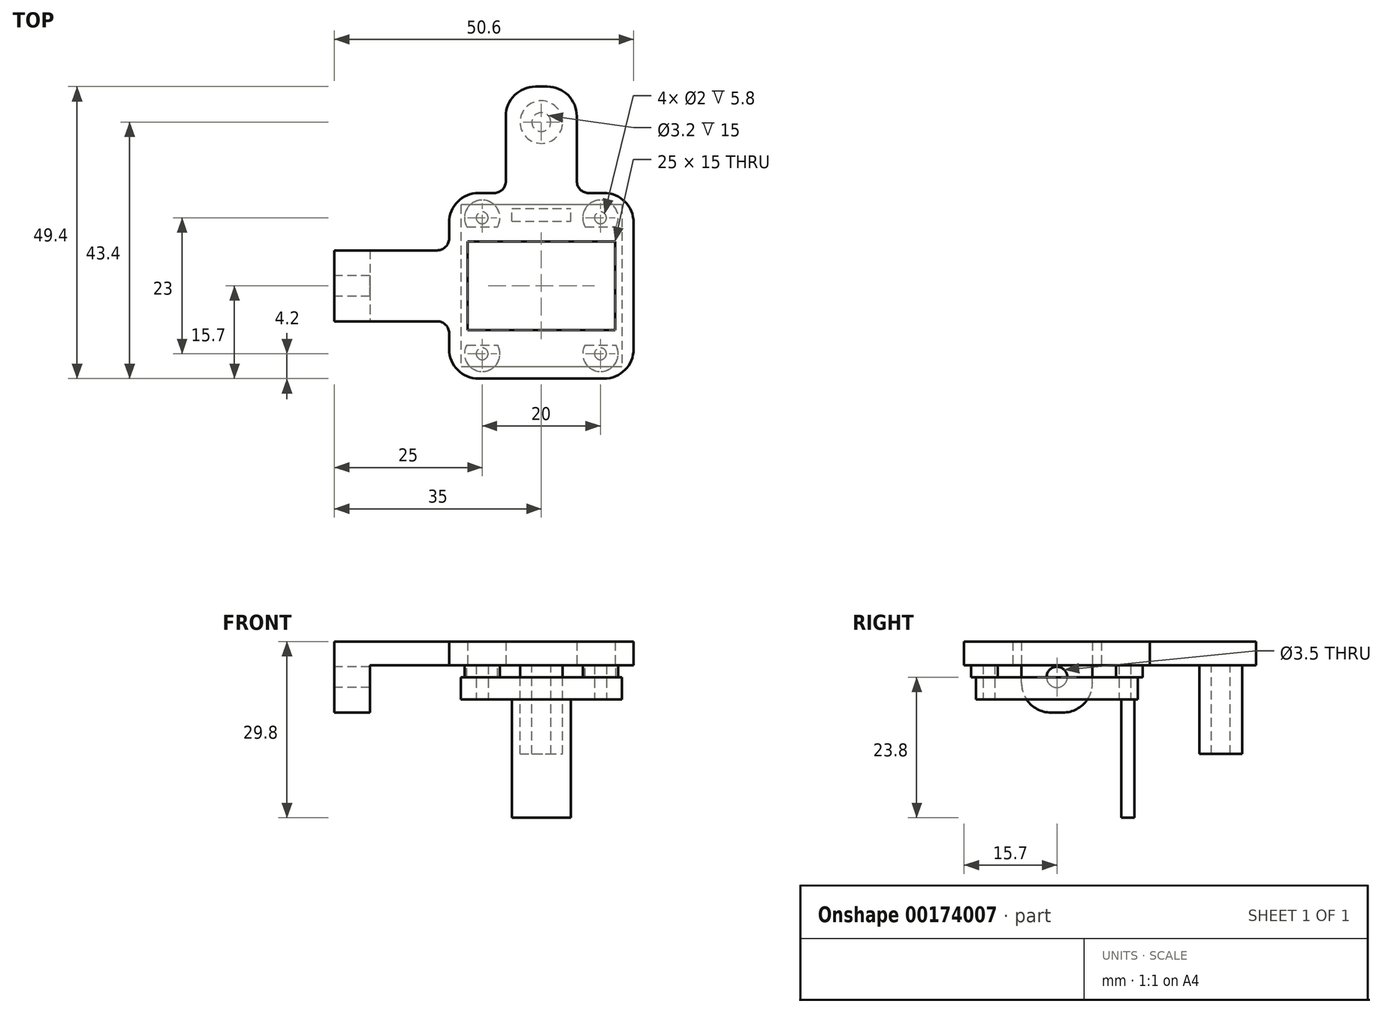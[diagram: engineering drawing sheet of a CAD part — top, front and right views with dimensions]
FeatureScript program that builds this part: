
annotation { "Feature Type Name" : "Feature", "Feature Type Description" : "" }
export const myFeature = defineFeature(function(context is Context, id is Id, definition is map)
    precondition{}
    {
        {
            assignVariable(context, id + "F0", {"name" : "wall", "anyValue" : 6});
        }
        {
            assignVariable(context, id + "F1", {"name" : "filletMinor", "anyValue" : 2});
        }
        {
            var Q0;
            Q0=qCreatedBy(makeId("Top.planeOp"),FACE);
            var sketch = newSketch(context, id + "F2", { "sketchPlane" : qUnion([Q0])});
            skLineSegment(sketch, "E0.bottom", {"start": v(13.6, 13.7) * mm, "end": v(-13.6, 13.7) * mm});
            skLineSegment(sketch, "E0.top", {"start": v(13.6, -13.7) * mm, "end": v(-13.6, -13.7) * mm});
            skLineSegment(sketch, "E0.left", {"start": v(13.6, 13.7) * mm, "end": v(13.6, -13.7) * mm});
            skLineSegment(sketch, "E0.right", {"start": v(-13.6, 13.7) * mm, "end": v(-13.6, -13.7) * mm});
            skPoint(sketch, "E0.middle", {"position": v(0, 0) * mm});
            skLineSegment(sketch, "E1.bottom", {"start": v(10, 11.5) * mm, "end": v(-10, 11.5) * mm, "construction": true});
            skLineSegment(sketch, "E1.top", {"start": v(10, -11.5) * mm, "end": v(-10, -11.5) * mm, "construction": true});
            skLineSegment(sketch, "E1.left", {"start": v(10, 11.5) * mm, "end": v(10, -11.5) * mm, "construction": true});
            skLineSegment(sketch, "E1.right", {"start": v(-10, 11.5) * mm, "end": v(-10, -11.5) * mm, "construction": true});
            skCircle(sketch, "E2", {"center": v(10, 11.5) * mm, "radius": 1 * mm});
            skCircle(sketch, "E3", {"center": v(-10, 11.5) * mm, "radius": 1 * mm});
            skCircle(sketch, "E4", {"center": v(-10, -11.5) * mm, "radius": 1 * mm});
            skCircle(sketch, "E5", {"center": v(10, -11.5) * mm, "radius": 1 * mm});
            skSolve(sketch);
        }
        {
            var Q0;
            Q0 = qSketchRegion(id + "F2", true);
            extrude(context, id + "F3", {"entities" : qUnion([Q0]), "depth" : 3.8 * mm});
        }
        {
            var Q0;
            Q0=makeQuery(id+"F3.opExtrude","CAP_FACE",FACE,{"disambiguationData":[OSD([sQuery(id+"F2.wireOp",EDGE,"E0.bottom"),sQuery(id+"F2.wireOp",EDGE,"E0.top"),sQuery(id+"F2.wireOp",EDGE,"E0.left"),sQuery(id+"F2.wireOp",EDGE,"E0.right")])],"isStart":true});
            var sketch = newSketch(context, id + "F4", { "sketchPlane" : qUnion([Q0])});
            skLineSegment(sketch, "E6.bottom", {"start": v(-5, -10.9) * mm, "end": v(5, -10.9) * mm});
            skLineSegment(sketch, "E6.top", {"start": v(-5, -13.1) * mm, "end": v(5, -13.1) * mm});
            skLineSegment(sketch, "E6.left", {"start": v(-5, -10.9) * mm, "end": v(-5, -13.1) * mm});
            skLineSegment(sketch, "E6.right", {"start": v(5, -10.9) * mm, "end": v(5, -13.1) * mm});
            skPoint(sketch, "E6.middle", {"position": v(0, -12) * mm});
            skSolve(sketch);
        }
        {
            var Q0;
            Q0 = qSketchRegion(id + "F4", true);
            extrude(context, id + "F5", {"entities" : qUnion([Q0]), "operationType" : NewBodyOperationType.ADD, "depth" : 20 * mm});
        }
        {
            var Q0;
            Q0=makeQuery(id+"F3.opExtrude","CAP_FACE",FACE,{"disambiguationData":[OSD([sQuery(id+"F2.wireOp",EDGE,"E0.bottom"),sQuery(id+"F2.wireOp",EDGE,"E0.top"),sQuery(id+"F2.wireOp",EDGE,"E0.left"),sQuery(id+"F2.wireOp",EDGE,"E0.right"),sQuery(id+"F2.wireOp",EDGE,"E2"),sQuery(id+"F2.wireOp",EDGE,"E3"),sQuery(id+"F2.wireOp",EDGE,"E4"),sQuery(id+"F2.wireOp",EDGE,"E5")])],"isStart":false});
            cPlane(context, id + "F6", {"entities" : qUnion([Q0]), "cplaneType" : CPlaneType.OFFSET, "offset" : 2 * mm, "width" : 150 * mm, "height" : 150 * mm});
        }
        {
            var Q0;
            Q0=qCreatedBy(id+"F6.planeOp",FACE);
            var sketch = newSketch(context, id + "F7", { "sketchPlane" : qUnion([Q0])});
            skLineSegment(sketch, "E7.bottom", {"start": v(12.5, 7.5) * mm, "end": v(-12.5, 7.5) * mm});
            skLineSegment(sketch, "E7.top", {"start": v(12.5, -7.5) * mm, "end": v(-12.5, -7.5) * mm});
            skLineSegment(sketch, "E7.left", {"start": v(12.5, 7.5) * mm, "end": v(12.5, -7.5) * mm});
            skLineSegment(sketch, "E7.right", {"start": v(-12.5, 7.5) * mm, "end": v(-12.5, -7.5) * mm});
            skPoint(sketch, "E7.middle", {"position": v(0, 0) * mm});
            skLineSegment(sketch, "E8.bottom", {"start": v(-15.6, 15.7) * mm, "end": v(-6, 15.7) * mm});
            skLineSegment(sketch, "E8.top", {"start": v(-15.6, -15.7) * mm, "end": v(15.6, -15.7) * mm});
            skLineSegment(sketch, "E8.left", {"start": v(-15.6, 15.7) * mm, "end": v(-15.6, 6) * mm});
            skLineSegment(sketch, "E8.right", {"start": v(15.6, 15.7) * mm, "end": v(15.6, -15.7) * mm});
            skLineSegment(sketch, "E9", {"start": v(-6, 15.7) * mm, "end": v(-6, 33.7) * mm});
            skLineSegment(sketch, "E10", {"start": v(-6, 33.7) * mm, "end": v(6, 33.7) * mm});
            skLineSegment(sketch, "E11", {"start": v(6, 33.7) * mm, "end": v(6, 15.7) * mm});
            skPoint(sketch, "E12", {"position": v(0, 33.7) * mm});
            skLineSegment(sketch, "E13.trimOffspring", {"start": v(6, 15.7) * mm, "end": v(15.6, 15.7) * mm});
            skLineSegment(sketch, "E14", {"start": v(-15.6, 6) * mm, "end": v(-35, 6) * mm});
            skLineSegment(sketch, "E15", {"start": v(-35, 6) * mm, "end": v(-35, -6) * mm});
            skLineSegment(sketch, "E16", {"start": v(-35, -6) * mm, "end": v(-15.6, -6) * mm});
            skPoint(sketch, "E17", {"position": v(-35, 0) * mm});
            skLineSegment(sketch, "E18.trimOffspring", {"start": v(-15.6, -6) * mm, "end": v(-15.6, -15.7) * mm});
            skSolve(sketch);
        }
        {
            var Q0;
            Q0 = qSketchRegion(id + "F7", true);
            extrude(context, id + "F8", {"entities" : qUnion([Q0]), "depth" : 4 * mm});
        }
        {
            var Q0;
            Q0=makeQuery(id+"F8.opExtrude","CAP_FACE",FACE,{"disambiguationData":[OSD([sQuery(id+"F7.wireOp",EDGE,"E7.bottom"),sQuery(id+"F7.wireOp",EDGE,"E7.top"),sQuery(id+"F7.wireOp",EDGE,"E7.left"),sQuery(id+"F7.wireOp",EDGE,"E7.right"),sQuery(id+"F7.wireOp",EDGE,"E8.bottom"),sQuery(id+"F7.wireOp",EDGE,"E8.top"),sQuery(id+"F7.wireOp",EDGE,"E8.left"),sQuery(id+"F7.wireOp",EDGE,"E8.right"),sQuery(id+"F7.wireOp",EDGE,"E9"),sQuery(id+"F7.wireOp",EDGE,"E10"),sQuery(id+"F7.wireOp",EDGE,"E11"),sQuery(id+"F7.wireOp",EDGE,"E13.trimOffspring")])],"isStart":true});
            var sketch = newSketch(context, id + "F9", { "sketchPlane" : qUnion([Q0])});
            skCircle(sketch, "E19", {"center": v(0, -27.7) * mm, "radius": 1.6 * mm});
            skPoint(sketch, "E19.centerSnap0", {"position": v(0, -33.7) * mm});
            skCircle(sketch, "E20", {"center": v(0, -27.7) * mm, "radius": 3.6 * mm});
            skLineSegment(sketch, "E21", {"start": v(0, -33.7) * mm, "end": v(0, -31.3) * mm, "construction": true});
            skLineSegment(sketch, "E22", {"start": v(-3.6, -27.7) * mm, "end": v(-6, -27.7) * mm, "construction": true});
            skSolve(sketch);
        }
        {
            var Q0;
            Q0 = qSketchRegion(id + "F9", true);
            extrude(context, id + "F10", {"entities" : qUnion([Q0]), "operationType" : NewBodyOperationType.ADD, "depth" : (12 + 3) * mm});
        }
        {
            var Q0;
            {var subQ0=sQuery(id+"F7.wireOp",EDGE,"E8.right");var subQ1=sQuery(id+"F7.wireOp",EDGE,"E8.left");var subQ2=sQuery(id+"F7.wireOp",EDGE,"E8.top");var subQ3=sQuery(id+"F7.wireOp",EDGE,"E8.bottom");var subQ4=sQuery(id+"F7.wireOp",EDGE,"E9");var subQ5=sQuery(id+"F7.wireOp",EDGE,"E7.left");var subQ6=sQuery(id+"F7.wireOp",EDGE,"E7.top");var subQ7=sQuery(id+"F7.wireOp",EDGE,"E10");var subQ8=sQuery(id+"F7.wireOp",EDGE,"E7.bottom");var subQ9=sQuery(id+"F7.wireOp",EDGE,"E7.right");var subQ10=sQuery(id+"F7.wireOp",EDGE,"E11");var subQ11=sQuery(id+"F7.wireOp",EDGE,"E13.trimOffspring");Q0=makeQuery(id+"F10.boolean.opBoolean","SPLIT",FACE,{"disambiguationData":[TD([makeQuery(id+"F8.opExtrude","SWEPT_FACE",FACE,{"disambiguationData":[OSD([subQ8])]})])],"derivedFrom":makeQuery(id+"F8.opExtrude","CAP_FACE",FACE,{"disambiguationData":[OSD([subQ8,subQ6,subQ5,subQ9,subQ3,subQ2,subQ1,subQ0,subQ4,subQ7,subQ10,subQ11])],"isStart":true})});}
            var sketch = newSketch(context, id + "F11", { "sketchPlane" : qUnion([Q0])});
            skCircle(sketch, "E23.0", {"center": v(-10, -11.5) * mm, "radius": 1 * mm});
            skCircle(sketch, "E23.1", {"center": v(-10, 11.5) * mm, "radius": 1 * mm});
            skCircle(sketch, "E23.2", {"center": v(10, 11.5) * mm, "radius": 1 * mm});
            skCircle(sketch, "E23.3", {"center": v(10, -11.5) * mm, "radius": 1 * mm});
            skArc(sketch, "E24", {"start": v(-7.4, 10) * mm, "mid": v(-10, 14.5) * mm, "end": v(-12.6, 10) * mm});
            skArc(sketch, "E25", {"start": v(-12.6, -10) * mm, "mid": v(-10, -14.5) * mm, "end": v(-7.4, -10) * mm});
            skArc(sketch, "E26", {"start": v(7.4, -10) * mm, "mid": v(10, -14.5) * mm, "end": v(12.6, -10) * mm});
            skArc(sketch, "E27", {"start": v(12.6, 10) * mm, "mid": v(10, 14.5) * mm, "end": v(7.4, 10) * mm});
            skLineSegment(sketch, "E28", {"start": v(-12.6, 10) * mm, "end": v(-7.4, 10) * mm});
            skLineSegment(sketch, "E29", {"start": v(7.4, 10) * mm, "end": v(12.6, 10) * mm});
            skLineSegment(sketch, "E30", {"start": v(-12.6, -10) * mm, "end": v(-7.4, -10) * mm});
            skLineSegment(sketch, "E31", {"start": v(7.4, -10) * mm, "end": v(12.6, -10) * mm});
            skSolve(sketch);
        }
        {
            var Q0;
            Q0 = qSketchRegion(id + "F11", true);
            var Q1;
            Q1=makeQuery(id+"F3.opExtrude","CAP_FACE",FACE,{"disambiguationData":[OSD([sQuery(id+"F2.wireOp",EDGE,"E0.bottom"),sQuery(id+"F2.wireOp",EDGE,"E0.top"),sQuery(id+"F2.wireOp",EDGE,"E0.left"),sQuery(id+"F2.wireOp",EDGE,"E0.right"),sQuery(id+"F2.wireOp",EDGE,"E2"),sQuery(id+"F2.wireOp",EDGE,"E3"),sQuery(id+"F2.wireOp",EDGE,"E4"),sQuery(id+"F2.wireOp",EDGE,"E5")])],"isStart":false});
            extrude(context, id + "F12", {"entities" : qUnion([Q0]), "operationType" : NewBodyOperationType.ADD, "endBound" : BoundingType.UP_TO_SURFACE, "endBoundEntityFace" : qUnion([Q1]), "depth" : 25 * mm});
        }
        {
            var Q0;
            {var subQ0=sQuery(id+"F7.wireOp",EDGE,"E16");var subQ3=sQuery(id+"F7.wireOp",EDGE,"E8.top");var subQ5=sQuery(id+"F7.wireOp",EDGE,"E18.trimOffspring");var subQ7=sQuery(id+"F7.wireOp",EDGE,"E15");var subQ9=sQuery(id+"F7.wireOp",EDGE,"E8.right");var subQ11=sQuery(id+"F7.wireOp",EDGE,"E13.trimOffspring");var subQ13=sQuery(id+"F7.wireOp",EDGE,"E11");var subQ15=sQuery(id+"F7.wireOp",EDGE,"E7.right");var subQ17=sQuery(id+"F7.wireOp",EDGE,"E14");var subQ19=sQuery(id+"F7.wireOp",EDGE,"E8.left");var subQ21=sQuery(id+"F7.wireOp",EDGE,"E7.bottom");var subQ22=makeQuery(id+"F8.opExtrude","SWEPT_FACE",FACE,{"disambiguationData":[OSD([subQ21])]});var subQ23=sQuery(id+"F7.wireOp",EDGE,"E8.bottom");var subQ25=sQuery(id+"F7.wireOp",EDGE,"E10");var subQ27=sQuery(id+"F7.wireOp",EDGE,"E7.top");var subQ29=sQuery(id+"F7.wireOp",EDGE,"E7.left");var subQ31=sQuery(id+"F7.wireOp",EDGE,"E9");Q0=makeQuery(id+"F12.boolean.opBoolean","SPLIT",FACE,{"disambiguationData":[TD([subQ22])],"derivedFrom":makeQuery(id+"F10.boolean.opBoolean","SPLIT",FACE,{"disambiguationData":[TD([subQ22])],"derivedFrom":makeQuery(id+"F8.opExtrude","CAP_FACE",FACE,{"disambiguationData":[OSD([subQ21,subQ27,subQ29,subQ15,subQ23,subQ3,subQ19,subQ9,subQ31,subQ25,subQ13,subQ11,subQ17,subQ7,subQ0,subQ5])],"isStart":true})})});}
            var sketch = newSketch(context, id + "F13", { "sketchPlane" : qUnion([Q0])});
            skLineSegment(sketch, "E32.bottom", {"start": v(-35, -6) * mm, "end": v(-29, -6) * mm});
            skLineSegment(sketch, "E32.top", {"start": v(-35, 6) * mm, "end": v(-29, 6) * mm});
            skLineSegment(sketch, "E32.left", {"start": v(-35, -6) * mm, "end": v(-35, 6) * mm});
            skLineSegment(sketch, "E32.right", {"start": v(-29, -6) * mm, "end": v(-29, 6) * mm});
            skSolve(sketch);
        }
        {
            var Q0;
            Q0 = qSketchRegion(id + "F13", true);
            extrude(context, id + "F14", {"entities" : qUnion([Q0]), "operationType" : NewBodyOperationType.ADD, "depth" : (2 * getVariable(context, 'wall') - 4) * mm});
        }
        {
            var Q0;
            Q0=makeQuery(id+"F14.boolean.opBoolean","MERGE",FACE,{"derivedFrom":[makeQuery(id+"F8.opExtrude","SWEPT_FACE",FACE,{"disambiguationData":[OSD([sQuery(id+"F7.wireOp",EDGE,"E15")])]}),makeQuery(id+"F14.opExtrude","SWEPT_FACE",FACE,{"disambiguationData":[OSD([sQuery(id+"F13.wireOp",EDGE,"E32.left")])]})]});
            var sketch = newSketch(context, id + "F15", { "sketchPlane" : qUnion([Q0])});
            skCircle(sketch, "E33", {"center": v(0, 3.8) * mm, "radius": 1.75 * mm});
            skPoint(sketch, "E33.centerSnap0", {"position": v(-6, 3.8) * mm});
            skPoint(sketch, "E33.centerSnap1", {"position": v(0, 9.8) * mm});
            skSolve(sketch);
        }
        {
            var Q0;
            Q0 = qSketchRegion(id + "F15", true);
            var Q1;
            Q1=makeQuery(id+"F14.opExtrude","SWEPT_FACE",FACE,{"disambiguationData":[OSD([sQuery(id+"F13.wireOp",EDGE,"E32.right")])]});
            extrude(context, id + "F16", {"entities" : qUnion([Q0]), "operationType" : NewBodyOperationType.REMOVE, "endBound" : BoundingType.UP_TO_SURFACE, "oppositeDirection" : true, "endBoundEntityFace" : qUnion([Q1]), "depth" : 25 * mm});
        }
        {
            var Q0;
            Q0=makeQuery(id+"F8.opExtrude","SWEPT_EDGE",EDGE,{"disambiguationData":[OSD([sQuery(id+"F7.wireOp",EDGE,"E8.bottom"),sQuery(id+"F7.wireOp",EDGE,"E8.left")])]});
            var Q1;
            Q1=makeQuery(id+"F8.opExtrude","SWEPT_EDGE",EDGE,{"disambiguationData":[OSD([sQuery(id+"F7.wireOp",EDGE,"E8.top"),sQuery(id+"F7.wireOp",EDGE,"E18.trimOffspring")])]});
            var Q2;
            Q2=makeQuery(id+"F8.opExtrude","SWEPT_EDGE",EDGE,{"disambiguationData":[OSD([sQuery(id+"F7.wireOp",EDGE,"E8.top"),sQuery(id+"F7.wireOp",EDGE,"E8.right")])]});
            var Q3;
            Q3=makeQuery(id+"F8.opExtrude","SWEPT_EDGE",EDGE,{"disambiguationData":[OSD([sQuery(id+"F7.wireOp",EDGE,"E9"),sQuery(id+"F7.wireOp",EDGE,"E10")])]});
            var Q4;
            Q4=makeQuery(id+"F8.opExtrude","SWEPT_EDGE",EDGE,{"disambiguationData":[OSD([sQuery(id+"F7.wireOp",EDGE,"E10"),sQuery(id+"F7.wireOp",EDGE,"E11")])]});
            var Q5;
            Q5=makeQuery(id+"F8.opExtrude","SWEPT_EDGE",EDGE,{"disambiguationData":[OSD([sQuery(id+"F7.wireOp",EDGE,"E8.bottom"),sQuery(id+"F7.wireOp",EDGE,"E8.left")])]});
            var Q6;
            Q6=makeQuery(id+"F8.opExtrude","SWEPT_EDGE",EDGE,{"disambiguationData":[OSD([sQuery(id+"F7.wireOp",EDGE,"E8.top"),sQuery(id+"F7.wireOp",EDGE,"E8.right")])]});
            var Q7;
            Q7=makeQuery(id+"F8.opExtrude","SWEPT_EDGE",EDGE,{"disambiguationData":[OSD([sQuery(id+"F7.wireOp",EDGE,"E8.right"),sQuery(id+"F7.wireOp",EDGE,"E13.trimOffspring")])]});
            var Q8;
            Q8=makeQuery(id+"F14.opExtrude","CAP_EDGE",EDGE,{"disambiguationData":[OSD([sQuery(id+"F13.wireOp",EDGE,"E32.bottom")])],"isStart":false});
            var Q9;
            Q9=makeQuery(id+"F14.opExtrude","CAP_EDGE",EDGE,{"disambiguationData":[OSD([sQuery(id+"F13.wireOp",EDGE,"E32.top")])],"isStart":false});
            fillet(context, id + "F17", {"entities" : qUnion([Q0, Q1, Q2, Q3, Q4, Q5, Q6, Q7, Q8, Q9]), "radius" : 5 * mm, "tangentPropagation" : true, "allowEdgeOverflow" : false});
        }
        {
            var Q0;
            Q0=makeQuery(id+"F8.opExtrude","SWEPT_EDGE",EDGE,{"disambiguationData":[OSD([sQuery(id+"F7.wireOp",EDGE,"E8.bottom"),sQuery(id+"F7.wireOp",EDGE,"E9")])]});
            var Q1;
            Q1=makeQuery(id+"F8.opExtrude","SWEPT_EDGE",EDGE,{"disambiguationData":[OSD([sQuery(id+"F7.wireOp",EDGE,"E11"),sQuery(id+"F7.wireOp",EDGE,"E13.trimOffspring")])]});
            var Q2;
            Q2=makeQuery(id+"F8.opExtrude","SWEPT_EDGE",EDGE,{"disambiguationData":[OSD([sQuery(id+"F7.wireOp",EDGE,"E16"),sQuery(id+"F7.wireOp",EDGE,"E18.trimOffspring")])]});
            var Q3;
            Q3=makeQuery(id+"F8.opExtrude","SWEPT_EDGE",EDGE,{"disambiguationData":[OSD([sQuery(id+"F7.wireOp",EDGE,"E8.left"),sQuery(id+"F7.wireOp",EDGE,"E14")])]});
            var Q4;
            Q4=makeQuery(id+"F10.opExtrude","CAP_EDGE",EDGE,{"disambiguationData":[OSD([sQuery(id+"F9.wireOp",EDGE,"E20")])],"isStart":true});
            fillet(context, id + "F18", {"entities" : qUnion([Q0, Q1, Q2, Q3, Q4]), "radius" : (getVariable(context, 'filletMinor')) * mm, "tangentPropagation" : true, "allowEdgeOverflow" : false});
        }
    });
